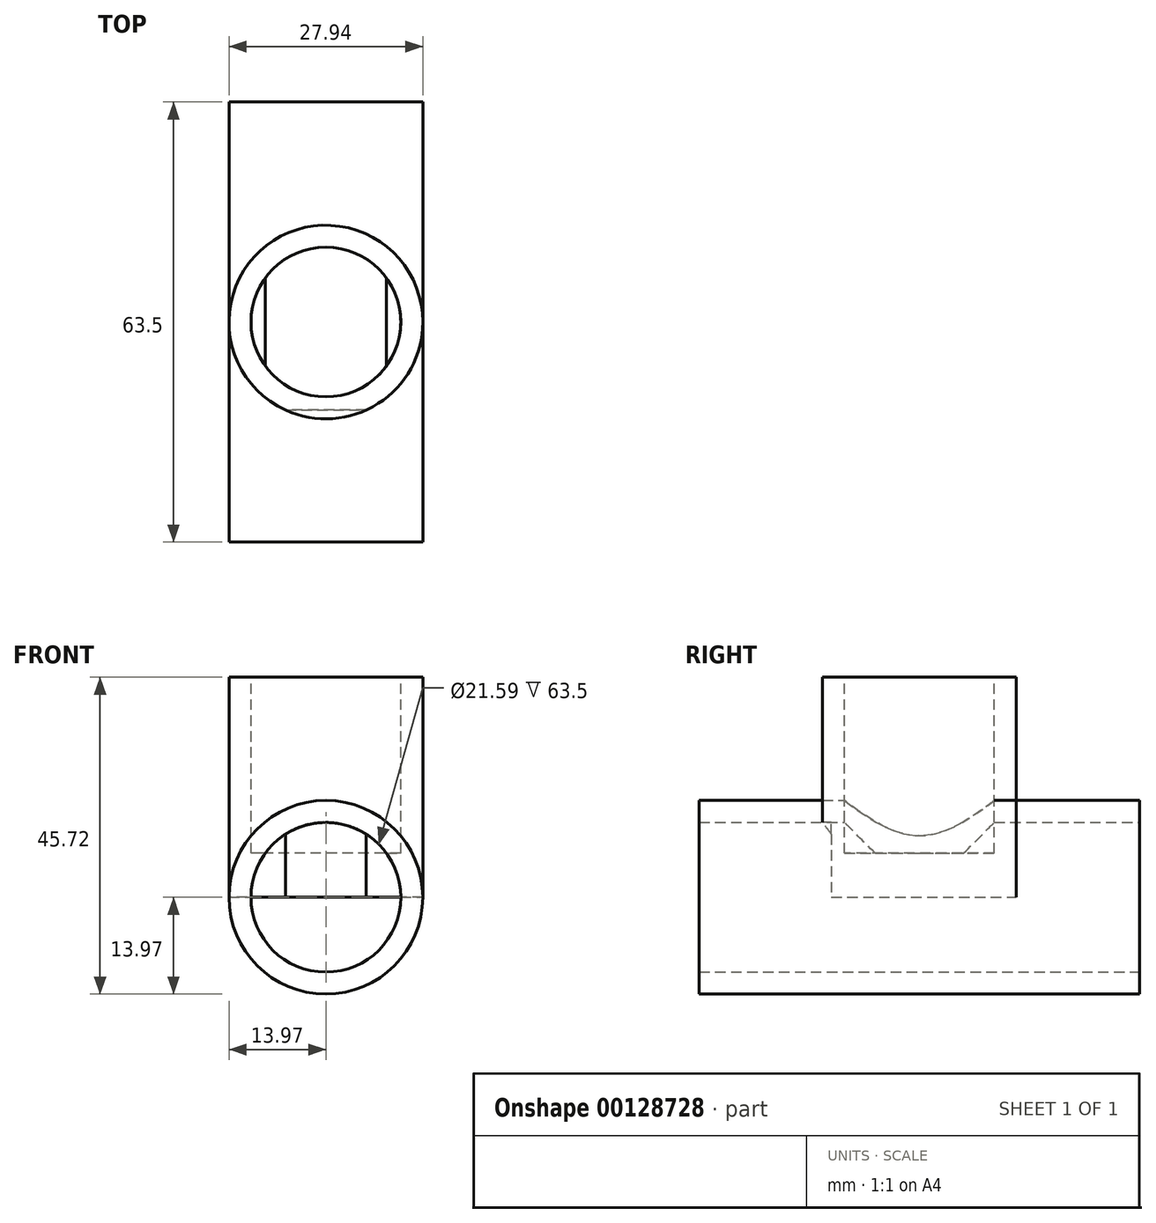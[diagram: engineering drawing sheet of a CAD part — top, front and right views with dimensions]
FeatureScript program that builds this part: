
annotation { "Feature Type Name" : "Feature", "Feature Type Description" : "" }
export const myFeature = defineFeature(function(context is Context, id is Id, definition is map)
    precondition{}
    {
        {
            var Q0;
            Q0=qCreatedBy(makeId("Front.planeOp"),FACE);
            var sketch = newSketch(context, id + "F0", { "sketchPlane" : qUnion([Q0])});
            skCircle(sketch, "E0", {"center": v(0, 0) * mm, "radius": 13.97 * mm});
            skSolve(sketch);
        }
        {
            var Q0;
            Q0 = qSketchRegion(id + "F0", true);
            extrude(context, id + "F1", {"entities" : qUnion([Q0]), "depth" : 63.5 * mm});
        }
        {
            var Q0;
            Q0=qCreatedBy(makeId("Top.planeOp"),FACE);
            var sketch = newSketch(context, id + "F2", { "sketchPlane" : qUnion([Q0])});
            skCircle(sketch, "E1", {"center": v(0, -31.75) * mm, "radius": 13.97 * mm});
            skSolve(sketch);
        }
        {
            var Q0;
            Q0=makeQuery(id+"F1.opExtrude","CAP_FACE",FACE,{"disambiguationData":[OSD([sQuery(id+"F0.wireOp",EDGE,"E0")])],"isStart":true});
            shell(context, id + "F3", {"entities" : qUnion([Q0]), "thickness" : 3.17 * mm});
        }
        {
            var Q0;
            Q0=makeQuery(id+"F1.opExtrude","CAP_FACE",FACE,{"disambiguationData":[OSD([sQuery(id+"F0.wireOp",EDGE,"E0")])],"isStart":false});
            var sketch = newSketch(context, id + "F4", { "sketchPlane" : qUnion([Q0])});
            skSolve(sketch);
        }
        {
            var Q0;
            Q0=makeQuery(id+"F1.opExtrude","CAP_FACE",FACE,{"disambiguationData":[OSD([sQuery(id+"F0.wireOp",EDGE,"E0")])],"isStart":false});
            var Q1;
            Q1=makeQuery(id+"F1.opExtrude","SWEPT_FACE",FACE,{"disambiguationData":[OSD([sQuery(id+"F0.wireOp",EDGE,"E0")])]});
            shell(context, id + "F5", {"entities" : qUnion([Q0, Q1]), "thickness" : 3.17 * mm});
        }
        {
            var Q0;
            Q0 = qSketchRegion(id + "F2", true);
            extrude(context, id + "F6", {"entities" : qUnion([Q0]), "depth" : 31.75 * mm});
        }
        {
            var Q0;
            Q0=makeQuery(id+"F4.imprint","IMPRINT",FACE,{"disambiguationData":[TD([[makeQuery(id+"F4.imprint","IMPRINT",EDGE,{"derivedFrom":makeQuery(id+"F1.opExtrude","CAP_EDGE",EDGE,{"disambiguationData":[OSD([sQuery(id+"F0.wireOp",EDGE,"E0")])],"isStart":false})}),1.0]])]});
            var sketch = newSketch(context, id + "F7", { "sketchPlane" : qUnion([Q0])});
            skCircle(sketch, "E2", {"center": v(0, 0) * mm, "radius": 10.8 * mm});
            skSolve(sketch);
        }
        {
            var Q0;
            Q0=makeQuery(id+"F6.opExtrude","CAP_FACE",FACE,{"disambiguationData":[OSD([sQuery(id+"F2.wireOp",EDGE,"E1")])],"isStart":false});
            var sketch = newSketch(context, id + "F8", { "sketchPlane" : qUnion([Q0])});
            skCircle(sketch, "E3", {"center": v(0, -31.75) * mm, "radius": 10.8 * mm});
            skSolve(sketch);
        }
        {
            var Q0;
            Q0 = qSketchRegion(id + "F8", true);
            extrude(context, id + "F9", {"entities" : qUnion([Q0]), "operationType" : NewBodyOperationType.REMOVE, "oppositeDirection" : true, "depth" : 25.4 * mm});
        }
        {
            var Q0;
            Q0 = qSketchRegion(id + "F7", true);
            extrude(context, id + "F10", {"entities" : qUnion([Q0]), "operationType" : NewBodyOperationType.REMOVE, "oppositeDirection" : true, "depth" : 19.05 * mm});
        }
    });
